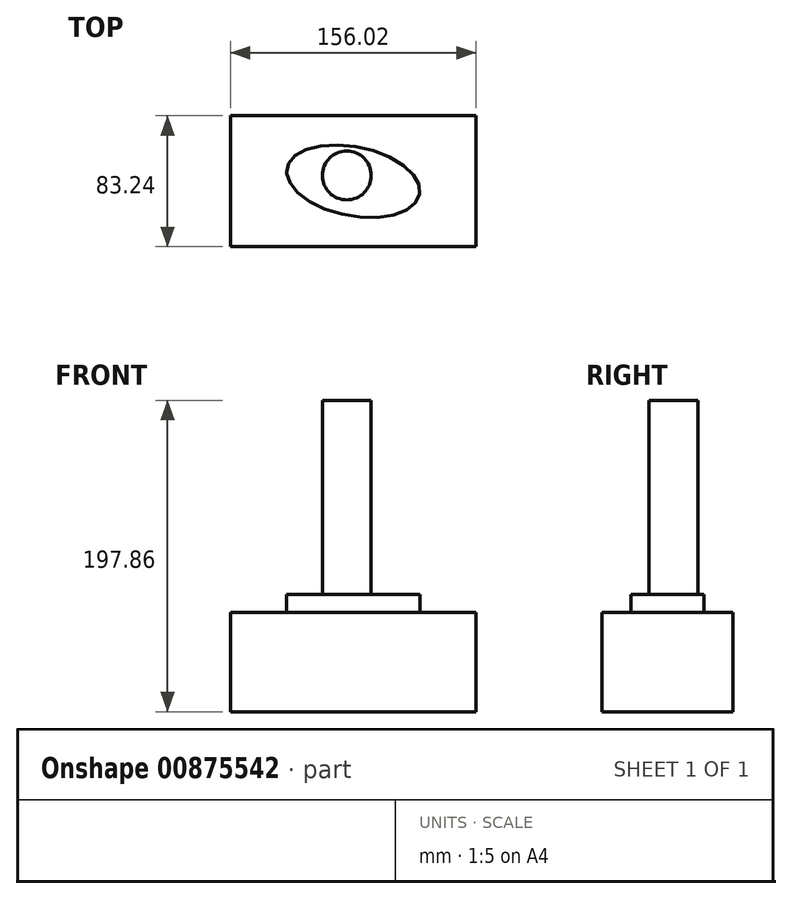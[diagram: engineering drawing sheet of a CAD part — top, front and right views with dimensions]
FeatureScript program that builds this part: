
annotation { "Feature Type Name" : "Feature", "Feature Type Description" : "" }
export const myFeature = defineFeature(function(context is Context, id is Id, definition is map)
    precondition{}
    {
        {
            var Q0;
            Q0=qCreatedBy(makeId("Top.planeOp"),FACE);
            var sketch = newSketch(context, id + "F0", { "sketchPlane" : qUnion([Q0])});
            skLineSegment(sketch, "E0.bottom", {"start": v(-78, 41.62) * mm, "end": v(78, 41.62) * mm});
            skLineSegment(sketch, "E0.top", {"start": v(-78, -41.62) * mm, "end": v(78, -41.62) * mm});
            skLineSegment(sketch, "E0.left", {"start": v(-78, 41.62) * mm, "end": v(-78, -41.62) * mm});
            skLineSegment(sketch, "E0.right", {"start": v(78, 41.62) * mm, "end": v(78, -41.62) * mm});
            skPoint(sketch, "E0.middle", {"position": v(0, 0) * mm});
            skSolve(sketch);
        }
        {
            var Q0;
            Q0=makeQuery(id+"F0.imprint","IMPRINT",FACE,{"disambiguationData":[TD([[makeQuery(id+"F0.imprint","IMPRINT",EDGE,{"derivedFrom":sQuery(id+"F0.wireOp",EDGE,"E0.bottom")}),-1.0]])]});
            extrude(context, id + "F1", {"entities" : qUnion([Q0]), "endBound" : BoundingType.SYMMETRIC, "depth" : 63.25 * mm, "offsetDistance" : 25.4 * mm});
        }
        {
            var Q0;
            Q0=makeQuery(id+"F1.opExtrude","CAP_FACE",FACE,{"disambiguationData":[OSD([sQuery(id+"F0.wireOp",EDGE,"E0.bottom"),sQuery(id+"F0.wireOp",EDGE,"E0.top"),sQuery(id+"F0.wireOp",EDGE,"E0.left"),sQuery(id+"F0.wireOp",EDGE,"E0.right")])],"isStart":false});
            var sketch = newSketch(context, id + "F2", { "sketchPlane" : qUnion([Q0])});
            skEllipse(sketch, "E1", {"center": v(0, 0) * mm, "majorRadius": 42.87 * mm, "minorRadius": 22 * mm, "majorAxis": v(0.98, -0.2)});
            skSolve(sketch);
        }
        {
            var Q0;
            Q0=makeQuery(id+"F2.imprint","IMPRINT",FACE,{"disambiguationData":[TD([[makeQuery(id+"F2.imprint","IMPRINT",EDGE,{"derivedFrom":sQuery(id+"F2.wireOp",EDGE,"E1")}),1.0]])]});
            extrude(context, id + "F3", {"entities" : qUnion([Q0]), "operationType" : NewBodyOperationType.ADD, "depth" : 11.18 * mm, "offsetDistance" : 25.4 * mm});
        }
        {
            var Q0;
            Q0=makeQuery(id+"F3.opExtrude","CAP_FACE",FACE,{"disambiguationData":[OSD([sQuery(id+"F2.wireOp",EDGE,"E1")])],"isStart":false});
            var sketch = newSketch(context, id + "F4", { "sketchPlane" : qUnion([Q0])});
            skCircle(sketch, "E2", {"center": v(-4.1, 3.68) * mm, "radius": 15.52 * mm});
            skSolve(sketch);
        }
        {
            var Q0;
            Q0 = qSketchRegion(id + "F4", true);
            extrude(context, id + "F5", {"entities" : qUnion([Q0]), "operationType" : NewBodyOperationType.ADD, "depth" : 123.44 * mm, "offsetDistance" : 25.4 * mm});
        }
    });
